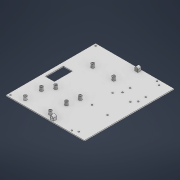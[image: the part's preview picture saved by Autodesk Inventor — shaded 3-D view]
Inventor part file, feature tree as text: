
AUTODESK INVENTOR PART (.ipt)
format: ipt  version: 2021 (Build 250183000, 183)  size: 282,112 bytes
history: native  units: mm
features: extrude x12, sketch x11, projected_geometry x7, other x1, fillet x1
ambient origin geometry x8: Origin, YZ Plane, XZ Plane, XY Plane, X Axis, Y Axis, Z Axis, Center Point
bodies: Volumenkörper1 (feature_tree)
feature tree (32):
  other  "Obenplatte_vorne"
  extrude  "Extrusion1"  Depth=200.0mm
  extrude  "Extrusion2"  Depth=2.0mm
  extrude  "Extrusion3"  Depth=42.0mm
  extrude  "Extrusion4"  Depth=5.0mm
  extrude  "Extrusion5"  TaperAngle=0.0deg  [1 undecoded]
  extrude  "Extrusion6"  Depth=10.5mm
  extrude  "Extrusion7"  Depth=3.2mm
  extrude  "Extrusion8"  Depth=23.0mm
  extrude  "Extrusion9"  Depth=23.0mm
  fillet  "Rundung1"  Radius=74.5mm
  extrude  "Extrusion10"  Depth=23.0mm
  extrude  "Extrusion11"  Depth=6.0mm
  extrude  "Extrusion12"  Depth=6.0mm
  sketch  "Skizze1"  dims[d0=175.0mm d1=200.0mm]
  sketch  "Skizze2"  dims[d2=2.0mm d3=0.0mm d4=3.2mm]
  sketch  "Skizze3"  dims[d5=3.2mm d6=42.0mm]
  sketch  "Skizze5"  dims[d7=5.0mm d9=5.0mm]
  projected_geometry  "Projizierte Kontur1"
  projected_geometry  "Projizierte Kontur2"
  projected_geometry  "Projizierte Kontur3"
  projected_geometry  "Projizierte Kontur4"
  sketch  "Skizze6"  dims[d10=42.0mm d11=0.0mm]
  sketch  "Skizze7"  dims[d35=3.2mm d36=10.5mm]
  sketch  "Skizze8"  dims[d37=23.0mm d38=3.2mm]
  sketch  "Skizze9"  dims[d39=74.5mm d40=23.0mm]
  sketch  "Skizze10"  dims[d41=3.2mm d42=23.0mm d43=74.5mm]
  sketch  "Skizze11"  dims[d44=3.2mm d45=23.0mm]
  sketch  "Skizze12"  dims[d46=10.5mm d47=3.2mm d48=60.0mm d49=77.0mm d50=3.2mm d51=60.0mm d52=77.0mm d53=60.0mm d54=0.0mm d55=5.0mm d56=33.0mm d57=53.34mm d58=101.6mm d59=40.0mm d60=7.0mm d61=86.36mm d62=50.8mm d63=7.0mm d64=90.17mm d65=50.8mm d66=7.0mm d67=96.52mm d68=50.8mm d69=7.0mm d70=87.63mm d71=50.8mm d72=7.0mm d73=0.0mm d74=4.0mm d75=4.0mm d76=4.0mm d77=4.0mm d78=5.0mm d79=0.0mm d80=3.2mm d81=3.2mm d82=15.0mm d83=15.0mm d84=35.0mm d85=17.0mm d86=5.0mm d87=0.0mm d88=3.2mm d89=3.2mm d90=50.0mm d91=50.0mm d92=35.0mm d94=17.0mm d95=103.5mm d96=7.0mm d97=7.0mm d98=2.2mm d99=9.0mm d100=0.0mm d101=4.0mm d102=5.0mm d103=3.5mm d104=5.0mm d105=0.0mm d107=4.0mm d108=3.5mm d109=5.0mm d110=5.0mm d111=0.0mm d112=3.5mm d113=20.0mm d114=40.0mm d115=8.0mm d116=10.0mm d117=0.0mm d118=7.0mm d119=7.0mm d120=7.0mm d121=7.0mm d122=30.0mm d123=30.0mm d126=56.0mm d127=36.0mm d128=56.0mm d129=36.0mm d130=7.0mm d131=0.0mm d132=4.3mm d133=4.3mm d134=4.3mm d135=4.3mm d136=6.0mm d137=0.0mm d138=13.0mm d139=13.0mm d140=35.0mm]
  projected_geometry  "Projizierte Kontur5"
  projected_geometry  "Projizierte Kontur6"
  projected_geometry  "Projizierte Kontur7"
note: 1 required parameter value undecoded (feature->parameter linkage not recoverable at this tier; creation-order binding heuristic only, values carry confidence <= 0.55)
